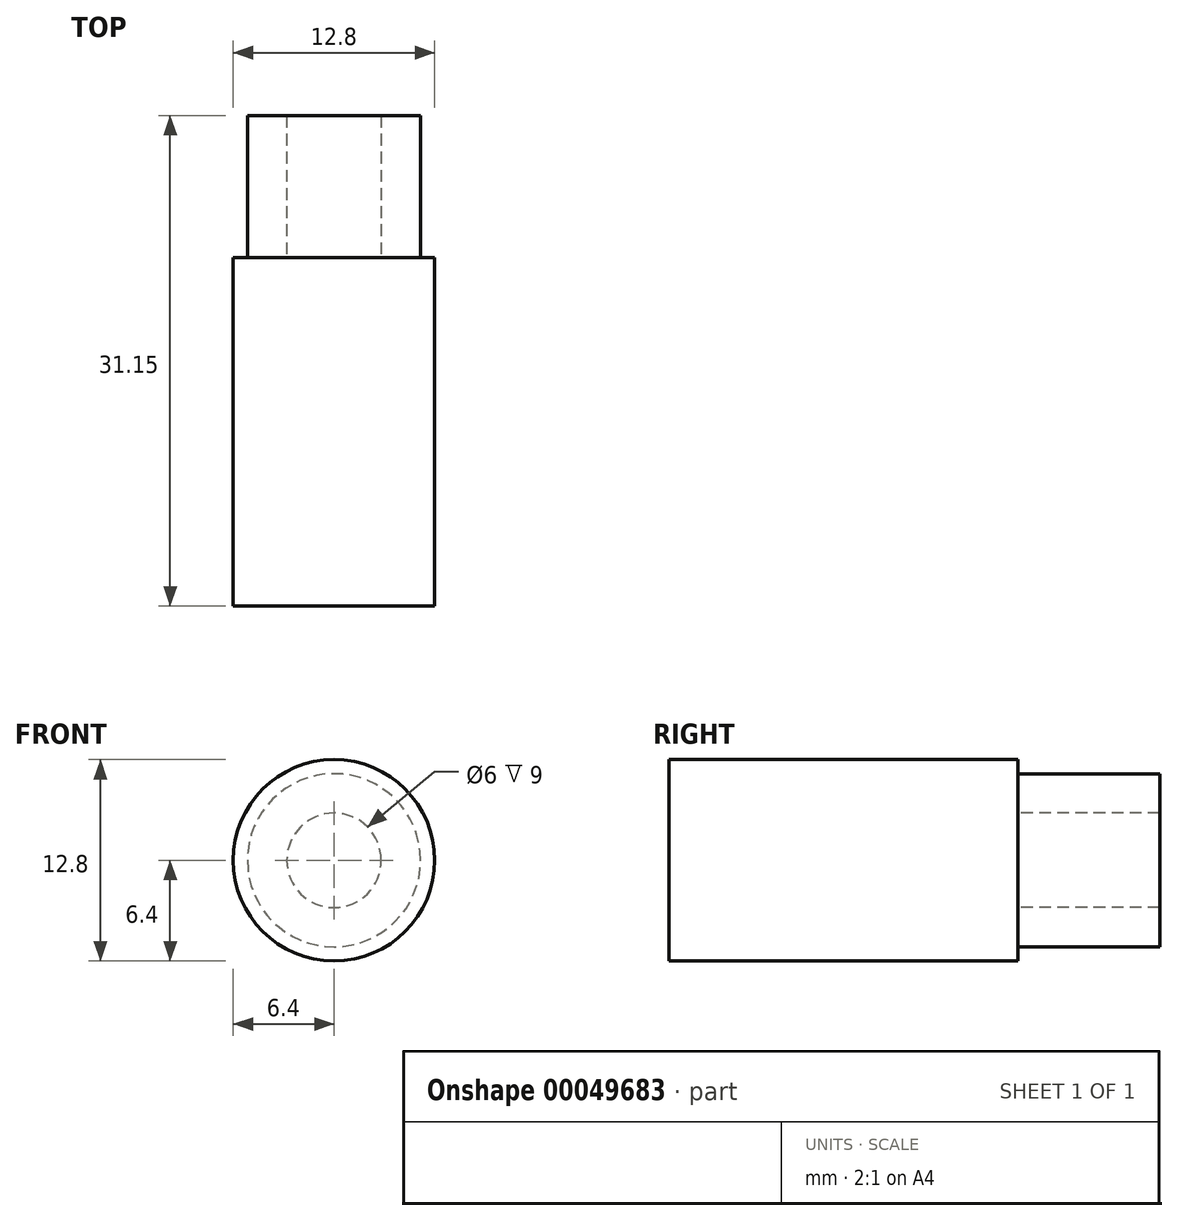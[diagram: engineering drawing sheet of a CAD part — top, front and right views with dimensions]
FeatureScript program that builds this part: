
annotation { "Feature Type Name" : "Feature", "Feature Type Description" : "" }
export const myFeature = defineFeature(function(context is Context, id is Id, definition is map)
    precondition{}
    {
        {
            var Q0;
            Q0=qCreatedBy(makeId("Front.planeOp"),FACE);
            var sketch = newSketch(context, id + "F0", { "sketchPlane" : qUnion([Q0])});
            skCircle(sketch, "E0", {"center": v(0, 0) * mm, "radius": 6.4 * mm});
            skSolve(sketch);
        }
        {
            var Q0;
            Q0 = qSketchRegion(id + "F0", true);
            var Q1;
            Q1=makeQuery(id+"F0.imprint","IMPRINT",FACE,{"disambiguationData":[TD([[makeQuery(id+"F0.imprint","IMPRINT",EDGE,{"derivedFrom":sQuery(id+"F0.wireOp",EDGE,"E0")}),1.0]])]});
            extrude(context, id + "F1", {"entities" : qUnion([Q0, Q1]), "depth" : 22.15 * mm});
        }
        {
            var Q0;
            Q0=makeQuery(id+"F1.opExtrude","CAP_FACE",FACE,{"disambiguationData":[OSD([sQuery(id+"F0.wireOp",EDGE,"E0")])],"isStart":true});
            var sketch = newSketch(context, id + "F2", { "sketchPlane" : qUnion([Q0])});
            skCircle(sketch, "E1", {"center": v(0, 0) * mm, "radius": 5.5 * mm});
            skCircle(sketch, "E2", {"center": v(0, 0) * mm, "radius": 3 * mm});
            skSolve(sketch);
        }
        {
            var Q0;
            Q0 = qSketchRegion(id + "F2", true);
            var Q1;
            Q1=makeQuery(id+"F2.imprint","IMPRINT",FACE,{"disambiguationData":[TD([[makeQuery(id+"F2.imprint","IMPRINT",EDGE,{"derivedFrom":sQuery(id+"F2.wireOp",EDGE,"E1")}),1.0]])]});
            extrude(context, id + "F3", {"entities" : qUnion([Q0, Q1]), "operationType" : NewBodyOperationType.ADD, "depth" : 9 * mm});
        }
    });
